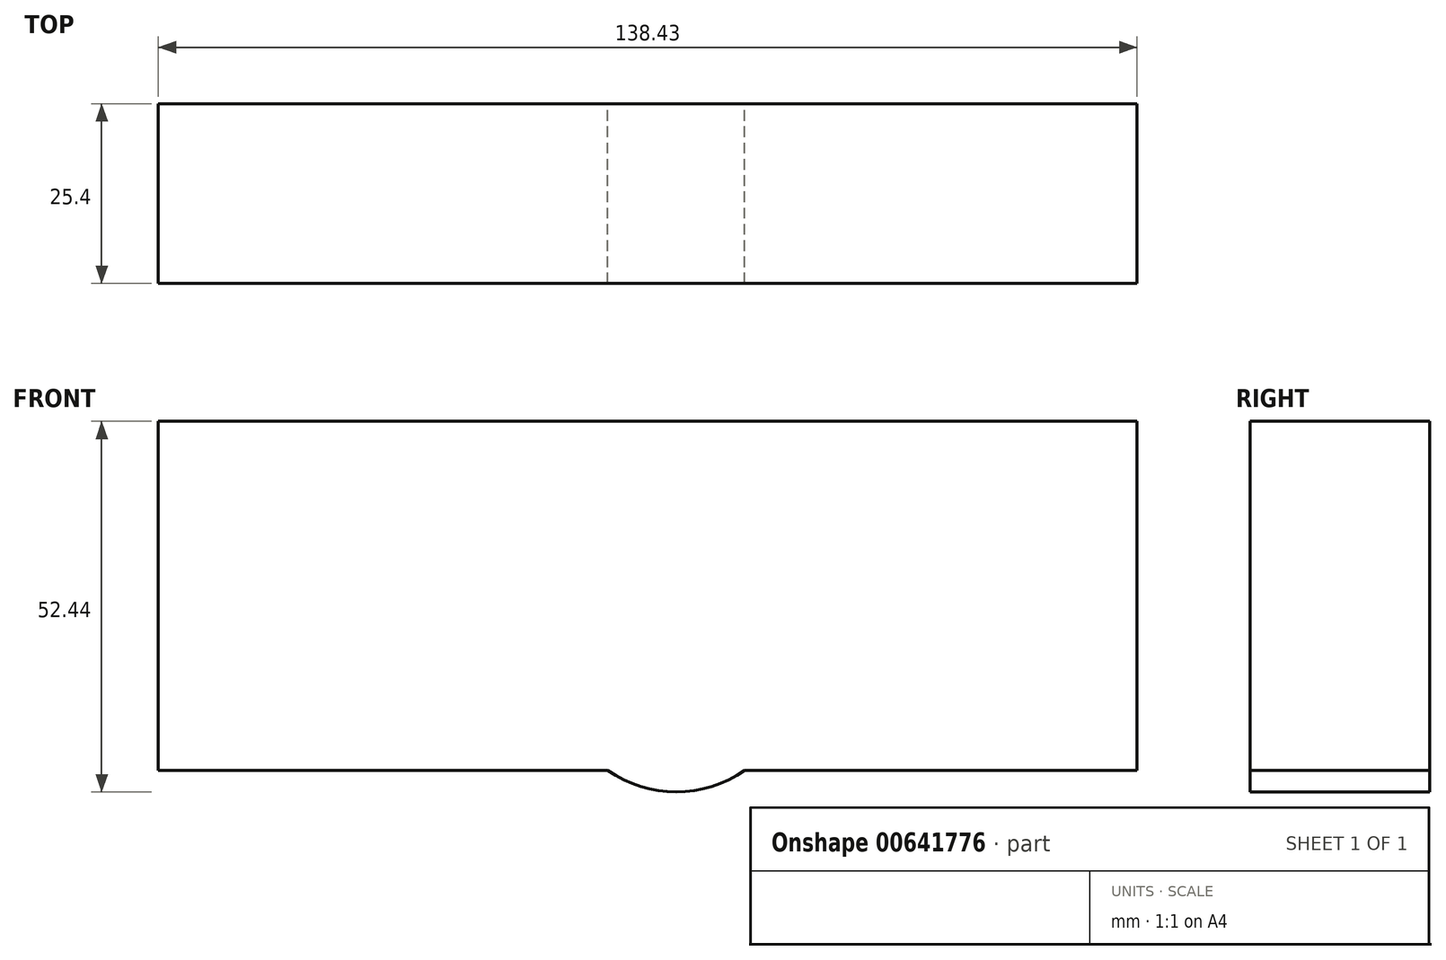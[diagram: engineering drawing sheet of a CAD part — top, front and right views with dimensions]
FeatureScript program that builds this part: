
annotation { "Feature Type Name" : "Feature", "Feature Type Description" : "" }
export const myFeature = defineFeature(function(context is Context, id is Id, definition is map)
    precondition{}
    {
        {
            var Q0;
            Q0=qCreatedBy(makeId("Front.planeOp"),FACE);
            var sketch = newSketch(context, id + "F0", { "sketchPlane" : qUnion([Q0])});
            skLineSegment(sketch, "E0.bottom", {"start": v(-17.14, 0) * mm, "end": v(121.29, 0) * mm});
            skLineSegment(sketch, "E0.top", {"start": v(-17.14, 49.4) * mm, "end": v(121.29, 49.4) * mm});
            skLineSegment(sketch, "E0.left", {"start": v(-17.14, 0) * mm, "end": v(-17.14, 49.4) * mm});
            skLineSegment(sketch, "E0.right", {"start": v(121.29, 0) * mm, "end": v(121.29, 49.4) * mm});
            skPoint(sketch, "E0.middle", {"position": v(52.07, 24.7) * mm});
            skSolve(sketch);
        }
        {
            var Q0;
            Q0=makeQuery(id+"F0.imprint","IMPRINT",FACE,{"disambiguationData":[TD([[makeQuery(id+"F0.imprint","IMPRINT",EDGE,{"derivedFrom":sQuery(id+"F0.wireOp",EDGE,"E0.bottom")}),1.0]])]});
            extrude(context, id + "F1", {"entities" : qUnion([Q0]), "depth" : 25.4 * mm, "offsetDistance" : 25.4 * mm});
        }
        {
            var Q0;
            Q0=qCreatedBy(makeId("Front.planeOp"),FACE);
            var sketch = newSketch(context, id + "F2", { "sketchPlane" : qUnion([Q0])});
            skCircle(sketch, "E1", {"center": v(56.12, 13.98) * mm, "radius": 17 * mm});
            skCircle(sketch, "E2", {"center": v(56.12, 13.98) * mm, "radius": 7.45 * mm, "construction": true});
            skSolve(sketch);
        }
        {
            var Q0;
            Q0 = qSketchRegion(id + "F2", true);
            extrude(context, id + "F3", {"entities" : qUnion([Q0]), "operationType" : NewBodyOperationType.ADD, "depth" : 25.4 * mm, "offsetDistance" : 25.4 * mm});
        }
        {
            var Q0;
            Q0=makeQuery(id+"F3.boolean.opBoolean","MERGE",FACE,{"derivedFrom":[makeQuery(id+"F1.opExtrude","CAP_FACE",FACE,{"disambiguationData":[OSD([sQuery(id+"F0.wireOp",EDGE,"E0.bottom"),sQuery(id+"F0.wireOp",EDGE,"E0.top"),sQuery(id+"F0.wireOp",EDGE,"E0.left"),sQuery(id+"F0.wireOp",EDGE,"E0.right")])],"isStart":false}),makeQuery(id+"F3.opExtrude","CAP_FACE",FACE,{"disambiguationData":[OSD([sQuery(id+"F2.wireOp",EDGE,"E1")])],"isStart":false})]});
            var sketch = newSketch(context, id + "F4", { "sketchPlane" : qUnion([Q0])});
            skPoint(sketch, "E3.oppositeSnap0", {"position": v(52.07, 49.4) * mm});
            skLineSegment(sketch, "E3.bottom", {"start": v(37.67, 27.72) * mm, "end": v(52.07, 27.72) * mm});
            skLineSegment(sketch, "E3.top", {"start": v(37.67, 34.13) * mm, "end": v(52.07, 34.13) * mm});
            skLineSegment(sketch, "E3.left", {"start": v(37.67, 27.72) * mm, "end": v(37.67, 34.13) * mm});
            skLineSegment(sketch, "E3.right", {"start": v(52.07, 27.72) * mm, "end": v(52.07, 34.13) * mm});
            skLineSegment(sketch, "E4.bottom", {"start": v(52.07, 27.72) * mm, "end": v(85.5, 27.72) * mm});
            skLineSegment(sketch, "E4.top", {"start": v(52.07, 49.4) * mm, "end": v(85.5, 49.4) * mm});
            skLineSegment(sketch, "E4.left", {"start": v(52.07, 27.72) * mm, "end": v(52.07, 49.4) * mm});
            skLineSegment(sketch, "E4.right", {"start": v(85.5, 27.72) * mm, "end": v(85.5, 49.4) * mm});
            skLineSegment(sketch, "E5.bottom", {"start": v(88.4, 23.99) * mm, "end": v(52.07, 23.99) * mm});
            skLineSegment(sketch, "E5.top", {"start": v(88.4, 27.72) * mm, "end": v(52.07, 27.72) * mm});
            skLineSegment(sketch, "E5.left", {"start": v(88.4, 23.99) * mm, "end": v(88.4, 27.72) * mm});
            skLineSegment(sketch, "E5.right", {"start": v(52.07, 23.99) * mm, "end": v(52.07, 27.72) * mm});
            skSolve(sketch);
        }
        {
            var Q0;
            Q0=sQuery(id+"F4.wireOp",EDGE,"E4.bottom");
            extrude(context, id + "F5", {"bodyType" : ToolBodyType.SURFACE, "surfaceEntities" : qUnion([Q0]), "depth" : 25.4 * mm, "offsetDistance" : 25.4 * mm});
        }
    });
